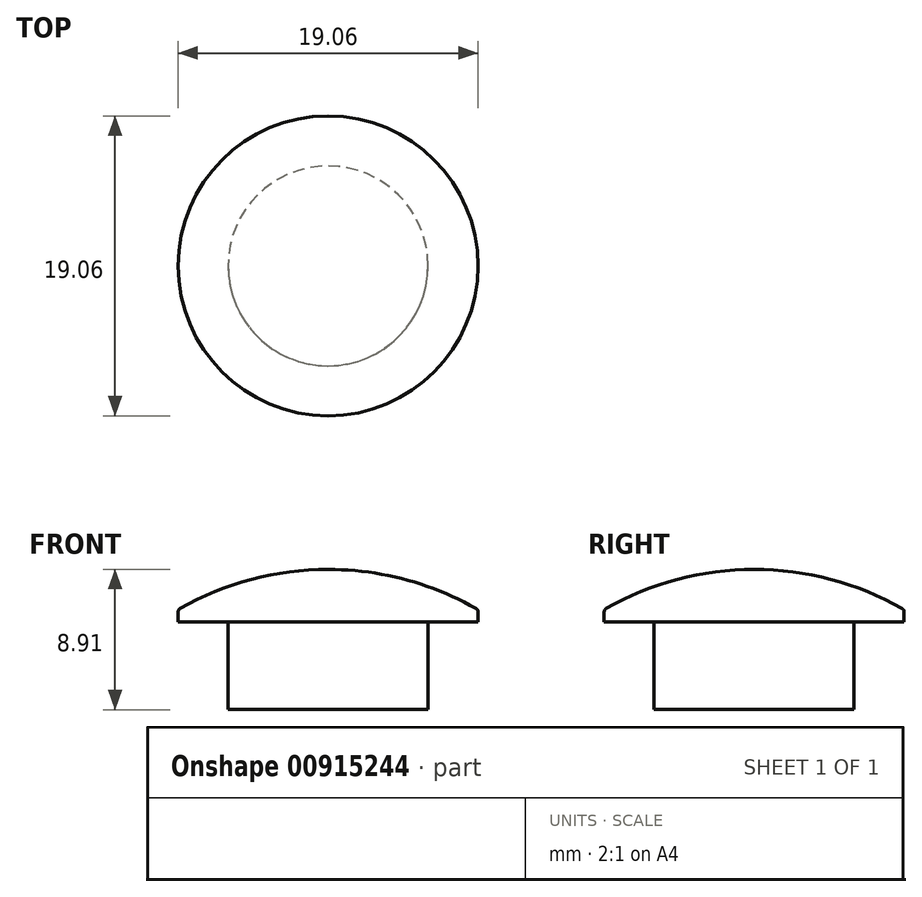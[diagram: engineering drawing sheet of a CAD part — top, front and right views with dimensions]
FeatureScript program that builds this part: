
annotation { "Feature Type Name" : "Feature", "Feature Type Description" : "" }
export const myFeature = defineFeature(function(context is Context, id is Id, definition is map)
    precondition{}
    {
        {
            var Q0;
            Q0=qCreatedBy(makeId("Top.planeOp"),FACE);
            var sketch = newSketch(context, id + "F0", { "sketchPlane" : qUnion([Q0])});
            skCircle(sketch, "E0", {"center": v(0, 0) * mm, "radius": 6.35 * mm});
            skSolve(sketch);
        }
        {
            var Q0;
            Q0=qSketchRegion(id+"F0",true);
            extrude(context, id + "F1", {"entities" : qUnion([Q0]), "endBound" : BoundingType.SYMMETRIC, "depth" : 6.35 * mm, "offsetDistance" : 25.4 * mm});
        }
        {
            var Q0;
            Q0=qCreatedBy(makeId("Front.planeOp"),FACE);
            var sketch = newSketch(context, id + "F2", { "sketchPlane" : qUnion([Q0])});
            skArc(sketch, "E1", {"start": v(9.52, 3.18) * mm, "mid": v(4.93, 5.08) * mm, "end": v(0, 5.73) * mm});
            skLineSegment(sketch, "E2", {"start": v(0, 2.38) * mm, "end": v(0, 5.73) * mm});
            skLineSegment(sketch, "E3", {"start": v(0, 2.38) * mm, "end": v(9.53, 2.38) * mm});
            skLineSegment(sketch, "E4", {"start": v(9.53, 2.38) * mm, "end": v(9.53, 3.18) * mm});
            skPoint(sketch, "E5.orphan", {"position": v(0, 2.38) * mm});
            skPoint(sketch, "E6.start.orphan", {"position": v(6.35, 3.18) * mm});
            skSolve(sketch);
        }
        {
            var Q0;
            Q0=makeQuery(id+"F2.imprint","IMPRINT",FACE,{"disambiguationData":[TD([[makeQuery(id+"F2.imprint","IMPRINT",EDGE,{"derivedFrom":sQuery(id+"F2.wireOp",EDGE,"E1")}),1.0]])]});
            var Q1;
            Q1=sQuery(id+"F2.wireOp",EDGE,"E2");
            revolve(context, id + "F3", {"operationType" : NewBodyOperationType.ADD, "surfaceOperationType" : NewSurfaceOperationType.NEW, "entities" : qUnion([Q0]), "axis" : qUnion([Q1]), "revolveType" : RevolveType.FULL});
        }
        {
            var Q0;
            Q0=makeQuery(id+"F3.opRevolve","SWEPT_EDGE",EDGE,{"disambiguationData":[OSD([sQuery(id+"F2.wireOp",EDGE,"E1"),sQuery(id+"F2.wireOp",EDGE,"E4")])]});
            fillet(context, id + "F4", {"entities" : qUnion([Q0]), "radius" : 0.25 * mm, "tangentPropagation" : true, "allowEdgeOverflow" : false});
        }
    });
